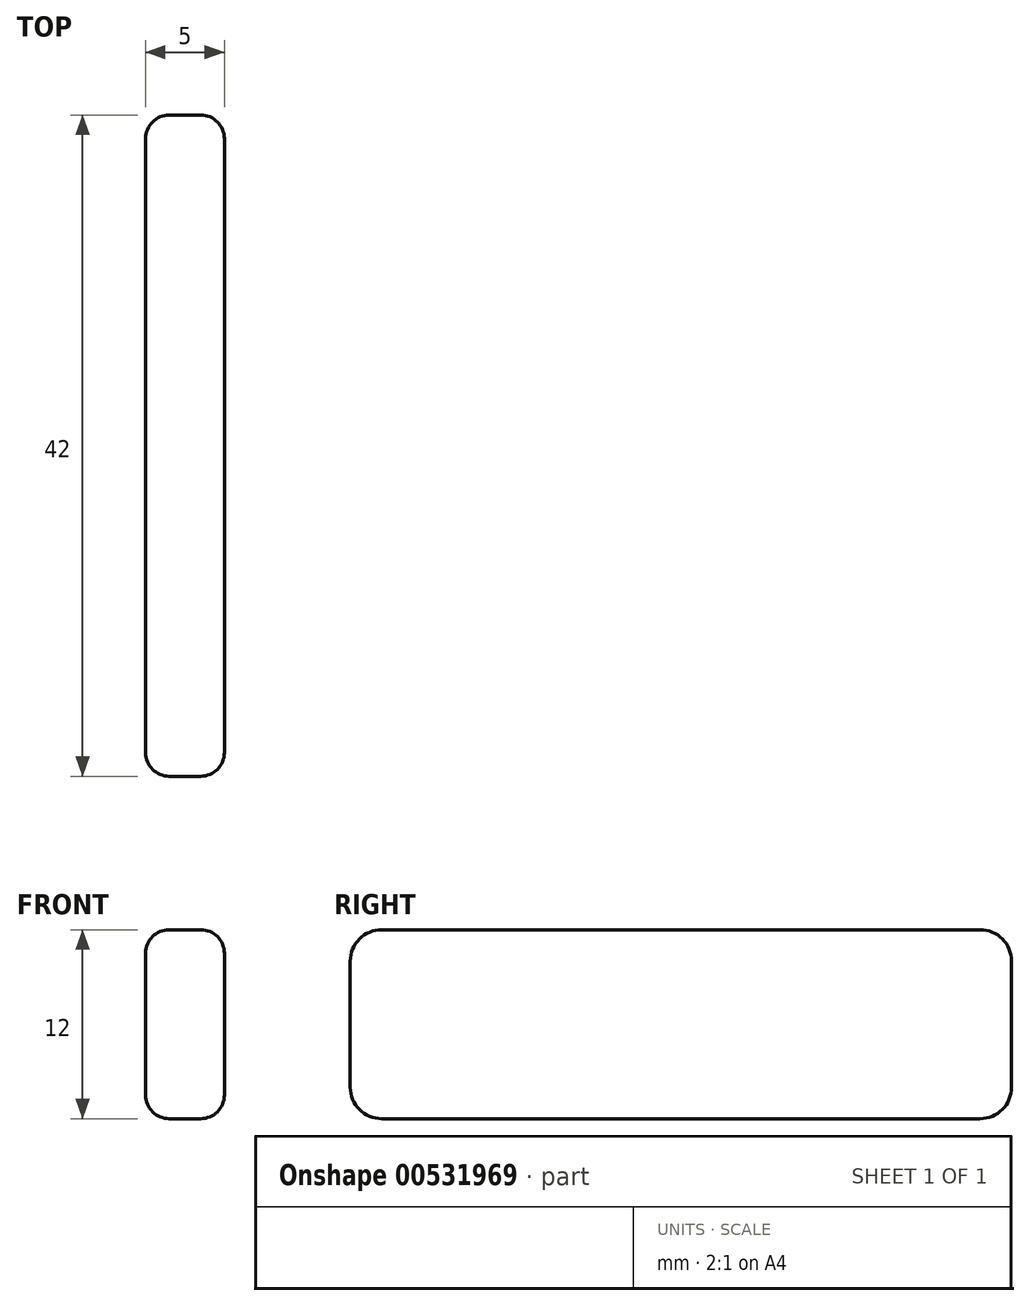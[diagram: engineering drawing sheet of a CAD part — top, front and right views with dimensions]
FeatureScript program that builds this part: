
annotation { "Feature Type Name" : "Feature", "Feature Type Description" : "" }
export const myFeature = defineFeature(function(context is Context, id is Id, definition is map)
    precondition{}
    {
        {
            var Q0;
            Q0=qCreatedBy(makeId("Right.planeOp"),FACE);
            var sketch = newSketch(context, id + "F0", { "sketchPlane" : qUnion([Q0])});
            skLineSegment(sketch, "E0.bottom", {"start": v(19, -6) * mm, "end": v(-19, -6) * mm});
            skLineSegment(sketch, "E0.top", {"start": v(19, 6) * mm, "end": v(-19, 6) * mm});
            skLineSegment(sketch, "E0.left", {"start": v(21, -4) * mm, "end": v(21, 4) * mm});
            skLineSegment(sketch, "E0.right", {"start": v(-21, -4) * mm, "end": v(-21, 4) * mm});
            skPoint(sketch, "E0.middle", {"position": v(0, 0) * mm});
            skPoint(sketch, "E1.visualSharp", {"position": v(-21, 6) * mm});
            skArc(sketch, "E1.filletArc", {"start": v(-19, 6) * mm, "mid": v(-20.41, 5.41) * mm, "end": v(-21, 4) * mm});
            skPoint(sketch, "E2.visualSharp", {"position": v(-21, -6) * mm});
            skArc(sketch, "E2.filletArc", {"start": v(-21, -4) * mm, "mid": v(-20.41, -5.41) * mm, "end": v(-19, -6) * mm});
            skPoint(sketch, "E3.visualSharp", {"position": v(21, 6) * mm});
            skArc(sketch, "E3.filletArc", {"start": v(21, 4) * mm, "mid": v(20.41, 5.41) * mm, "end": v(19, 6) * mm});
            skPoint(sketch, "E4.visualSharp", {"position": v(21, -6) * mm});
            skArc(sketch, "E4.filletArc", {"start": v(19, -6) * mm, "mid": v(20.41, -5.41) * mm, "end": v(21, -4) * mm});
            skSolve(sketch);
        }
        {
            var Q0;
            Q0=qSketchRegion(id+"F0",true);
            extrude(context, id + "F1", {"entities" : qUnion([Q0]), "depth" : 5 * mm});
        }
        {
            var Q0;
            Q0=makeQuery(id+"F1.opExtrude","CAP_EDGE",EDGE,{"disambiguationData":[OSD([sQuery(id+"F0.wireOp",EDGE,"E2.filletArc")])],"isStart":false});
            var Q1;
            Q1=makeQuery(id+"F1.opExtrude","CAP_EDGE",EDGE,{"disambiguationData":[OSD([sQuery(id+"F0.wireOp",EDGE,"E2.filletArc")])],"isStart":true});
            fillet(context, id + "F2", {"entities" : qUnion([Q0, Q1]), "radius" : 1.5 * mm, "tangentPropagation" : true, "allowEdgeOverflow" : false});
        }
    });
